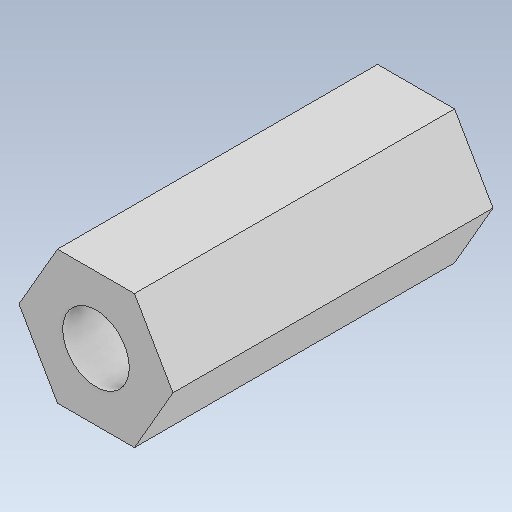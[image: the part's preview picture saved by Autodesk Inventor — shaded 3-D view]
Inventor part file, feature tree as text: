
AUTODESK INVENTOR PART (.ipt)
format: ipt  version: 2021 (Build 250183000, 183)  size: 98,816 bytes
history: native  units: mm
features: extrude x2, sketch x2
ambient origin geometry x8: Origin, YZ Plane, XZ Plane, XY Plane, X Axis, Y Axis, Z Axis, Center Point
bodies: Solid1 (feature_tree)
feature tree (4):
  extrude  "Extrusion1"  Depth=12.0mm TaperAngle=0.0deg
  extrude  "Extrusion3"  Depth=7.0mm TaperAngle=0.0deg
  sketch  "Sketch1"  dims[d0=5.0mm d1=12.0mm d2=0.0mm]
  sketch  "Sketch3"  dims[d6=2.5mm d7=7.0mm d8=0.0mm]
